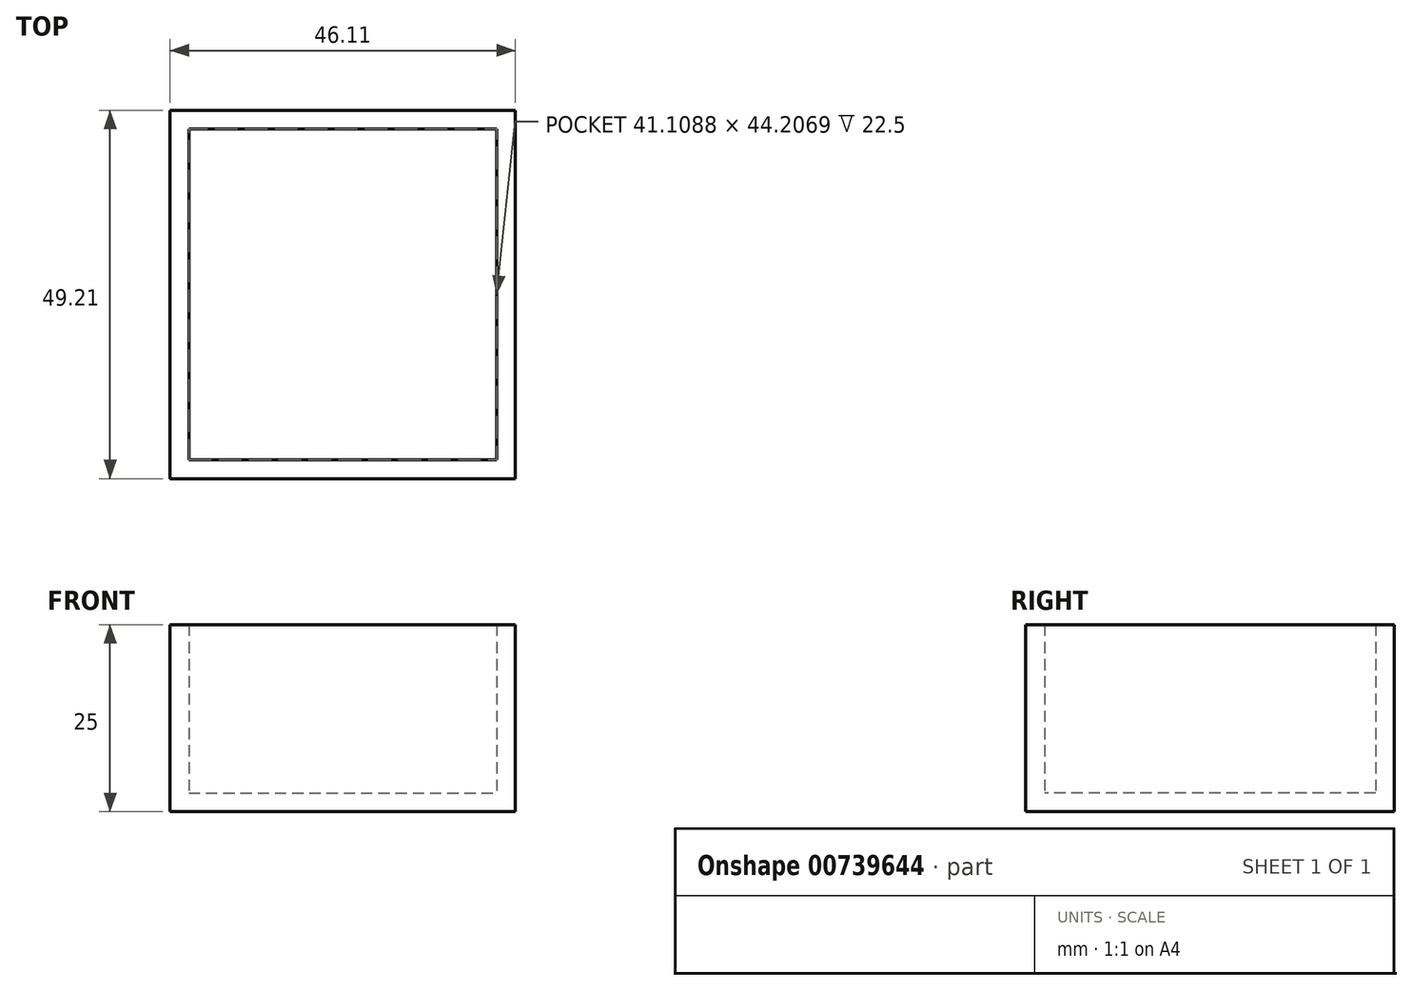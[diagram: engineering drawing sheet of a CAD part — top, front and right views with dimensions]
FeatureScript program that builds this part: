
annotation { "Feature Type Name" : "Feature", "Feature Type Description" : "" }
export const myFeature = defineFeature(function(context is Context, id is Id, definition is map)
    precondition{}
    {
        {
            var Q0;
            Q0=qCreatedBy(makeId("Top.planeOp"),FACE);
            var sketch = newSketch(context, id + "F0", { "sketchPlane" : qUnion([Q0])});
            skLineSegment(sketch, "E0.bottom", {"start": v(0, 0) * mm, "end": v(46.1, 0) * mm});
            skLineSegment(sketch, "E0.top", {"start": v(0, -49.2) * mm, "end": v(46.1, -49.2) * mm});
            skLineSegment(sketch, "E0.left", {"start": v(0, 0) * mm, "end": v(0, -49.2) * mm});
            skLineSegment(sketch, "E0.right", {"start": v(46.1, 0) * mm, "end": v(46.1, -49.2) * mm});
            skSolve(sketch);
        }
        {
            var Q0;
            Q0=qSketchRegion(id+"F0",true);
            extrude(context, id + "F1", {"entities" : qUnion([Q0]), "depth" : 25 * mm, "offsetDistance" : 25 * mm});
        }
        {
            var Q0;
            Q0=makeQuery(id+"F1.opExtrude","CAP_FACE",FACE,{"disambiguationData":[OSD([sQuery(id+"F0.wireOp",EDGE,"E0.bottom"),sQuery(id+"F0.wireOp",EDGE,"E0.top"),sQuery(id+"F0.wireOp",EDGE,"E0.left"),sQuery(id+"F0.wireOp",EDGE,"E0.right")])],"isStart":false});
            shell(context, id + "F2", {"entities" : qUnion([Q0]), "thickness" : 2.5 * mm});
        }
    });
